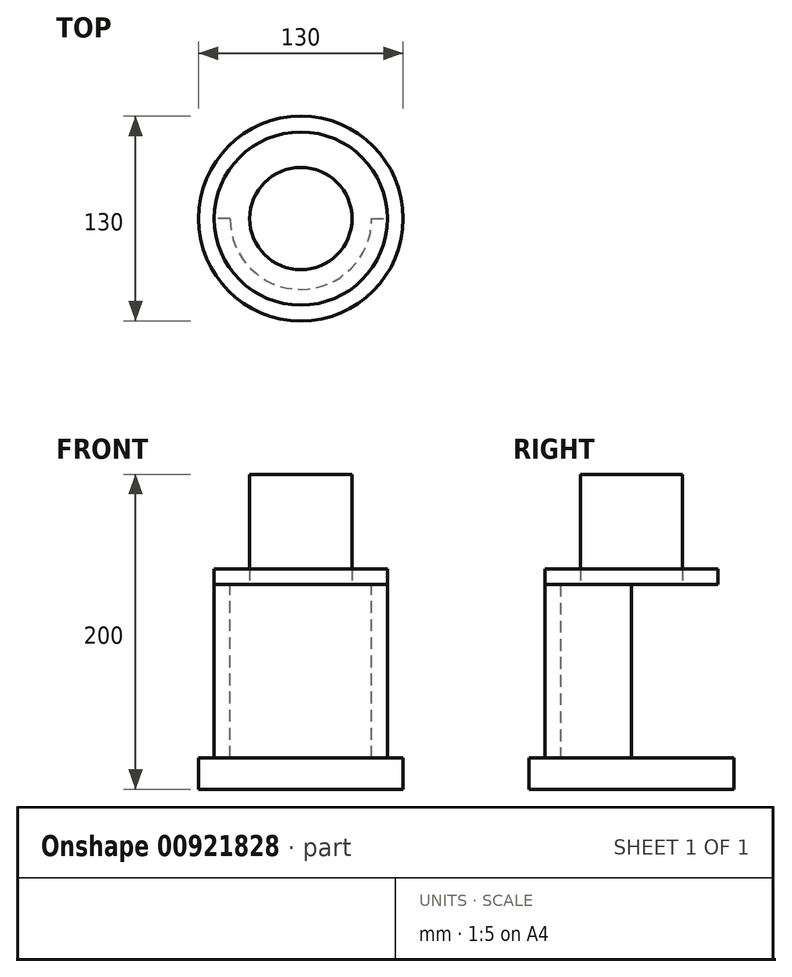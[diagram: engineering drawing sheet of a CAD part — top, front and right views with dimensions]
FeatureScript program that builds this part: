
annotation { "Feature Type Name" : "Feature", "Feature Type Description" : "" }
export const myFeature = defineFeature(function(context is Context, id is Id, definition is map)
    precondition{}
    {
        {
            var Q0;
            Q0=qCreatedBy(makeId("Top.planeOp"),FACE);
            var sketch = newSketch(context, id + "F0", { "sketchPlane" : qUnion([Q0])});
            skCircle(sketch, "E0", {"center": v(0, 0) * mm, "radius": 55 * mm});
            skCircle(sketch, "E1", {"center": v(0, 0) * mm, "radius": 45 * mm});
            skSolve(sketch);
        }
        {
            var Q0;
            Q0 = qSketchRegion(id + "F0", true);
            extrude(context, id + "F1", {"entities" : qUnion([Q0]), "endBound" : BoundingType.SYMMETRIC, "depth" : 110 * mm, "offsetDistance" : 25 * mm});
        }
        {
            var Q0;
            Q0=makeQuery(id+"F1.opExtrude","CAP_FACE",FACE,{"disambiguationData":[OSD([sQuery(id+"F0.wireOp",EDGE,"E0"),sQuery(id+"F0.wireOp",EDGE,"E1")])],"isStart":false});
            var sketch = newSketch(context, id + "F2", { "sketchPlane" : qUnion([Q0])});
            skArc(sketch, "E2", {"start": v(45, 0) * mm, "mid": v(0, 45) * mm, "end": v(-45, 0) * mm});
            skArc(sketch, "E3", {"start": v(60, 0) * mm, "mid": v(0, 60) * mm, "end": v(-60, 0) * mm});
            skLineSegment(sketch, "E4", {"start": v(45, 0) * mm, "end": v(60, 0) * mm});
            skLineSegment(sketch, "E5", {"start": v(-45, 0) * mm, "end": v(-60, 0) * mm});
            skSolve(sketch);
        }
        {
            var Q0;
            Q0 = qSketchRegion(id + "F2", true);
            extrude(context, id + "F3", {"entities" : qUnion([Q0]), "operationType" : NewBodyOperationType.REMOVE, "oppositeDirection" : true, "depth" : 130 * mm, "offsetDistance" : 25 * mm});
        }
        {
            var Q0;
            Q0=makeQuery(id+"F1.opExtrude","CAP_FACE",FACE,{"disambiguationData":[OSD([sQuery(id+"F0.wireOp",EDGE,"E0"),sQuery(id+"F0.wireOp",EDGE,"E1")])],"isStart":false});
            cPlane(context, id + "F4", {"entities" : qUnion([Q0]), "cplaneType" : CPlaneType.OFFSET, "offset" : 0 * mm, "oppositeDirection" : true, "width" : 150 * mm, "height" : 150 * mm});
        }
        {
            var Q0;
            Q0=qCreatedBy(id+"F4.planeOp",FACE);
            var sketch = newSketch(context, id + "F5", { "sketchPlane" : qUnion([Q0])});
            skCircle(sketch, "E6", {"center": v(0, 0) * mm, "radius": 55 * mm});
            skSolve(sketch);
        }
        {
            var Q0;
            Q0 = qSketchRegion(id + "F5", true);
            var Q1;
            Q1=makeQuery(id+"F1.opExtrude","CAP_FACE",FACE,{"disambiguationData":[OSD([sQuery(id+"F0.wireOp",EDGE,"E0"),sQuery(id+"F0.wireOp",EDGE,"E1")])],"isStart":false});
            extrude(context, id + "F6", {"entities" : qUnion([Q0]), "depth" : 10 * mm, "endBoundEntityFace" : qUnion([Q1]), "hasOffset" : true, "offsetDistance" : 10 * mm});
        }
        {
            var Q0;
            Q0=qCreatedBy(id+"F4.planeOp",FACE);
            var sketch = newSketch(context, id + "F7", { "sketchPlane" : qUnion([Q0])});
            skCircle(sketch, "E7", {"center": v(0, 0) * mm, "radius": 32.5 * mm});
            skSolve(sketch);
        }
        {
            var Q0;
            Q0 = qSketchRegion(id + "F7", true);
            extrude(context, id + "F8", {"entities" : qUnion([Q0]), "depth" : 70 * mm, "offsetDistance" : 25 * mm});
        }
        {
            var Q0;
            Q0=makeQuery(id+"F1.opExtrude","CAP_FACE",FACE,{"disambiguationData":[OSD([sQuery(id+"F0.wireOp",EDGE,"E0"),sQuery(id+"F0.wireOp",EDGE,"E1")])],"isStart":true});
            cPlane(context, id + "F9", {"entities" : qUnion([Q0]), "cplaneType" : CPlaneType.OFFSET, "offset" : 0 * mm, "width" : 150 * mm, "height" : 150 * mm});
        }
        {
            var Q0;
            Q0=qCreatedBy(makeId("Top.planeOp"),FACE);
            cPlane(context, id + "F10", {"entities" : qUnion([Q0]), "cplaneType" : CPlaneType.OFFSET, "offset" : 76 * mm, "oppositeDirection" : true, "width" : 150 * mm, "height" : 150 * mm});
        }
        {
            var Q0;
            Q0=qCreatedBy(id+"F9.planeOp",FACE);
            var sketch = newSketch(context, id + "F11", { "sketchPlane" : qUnion([Q0])});
            skCircle(sketch, "E8", {"center": v(0, 0) * mm, "radius": 65 * mm});
            skSolve(sketch);
        }
        {
            var Q0;
            Q0 = qSketchRegion(id + "F11", true);
            extrude(context, id + "F12", {"entities" : qUnion([Q0]), "operationType" : NewBodyOperationType.ADD, "depth" : 20 * mm, "offsetDistance" : 25 * mm});
        }
    });
